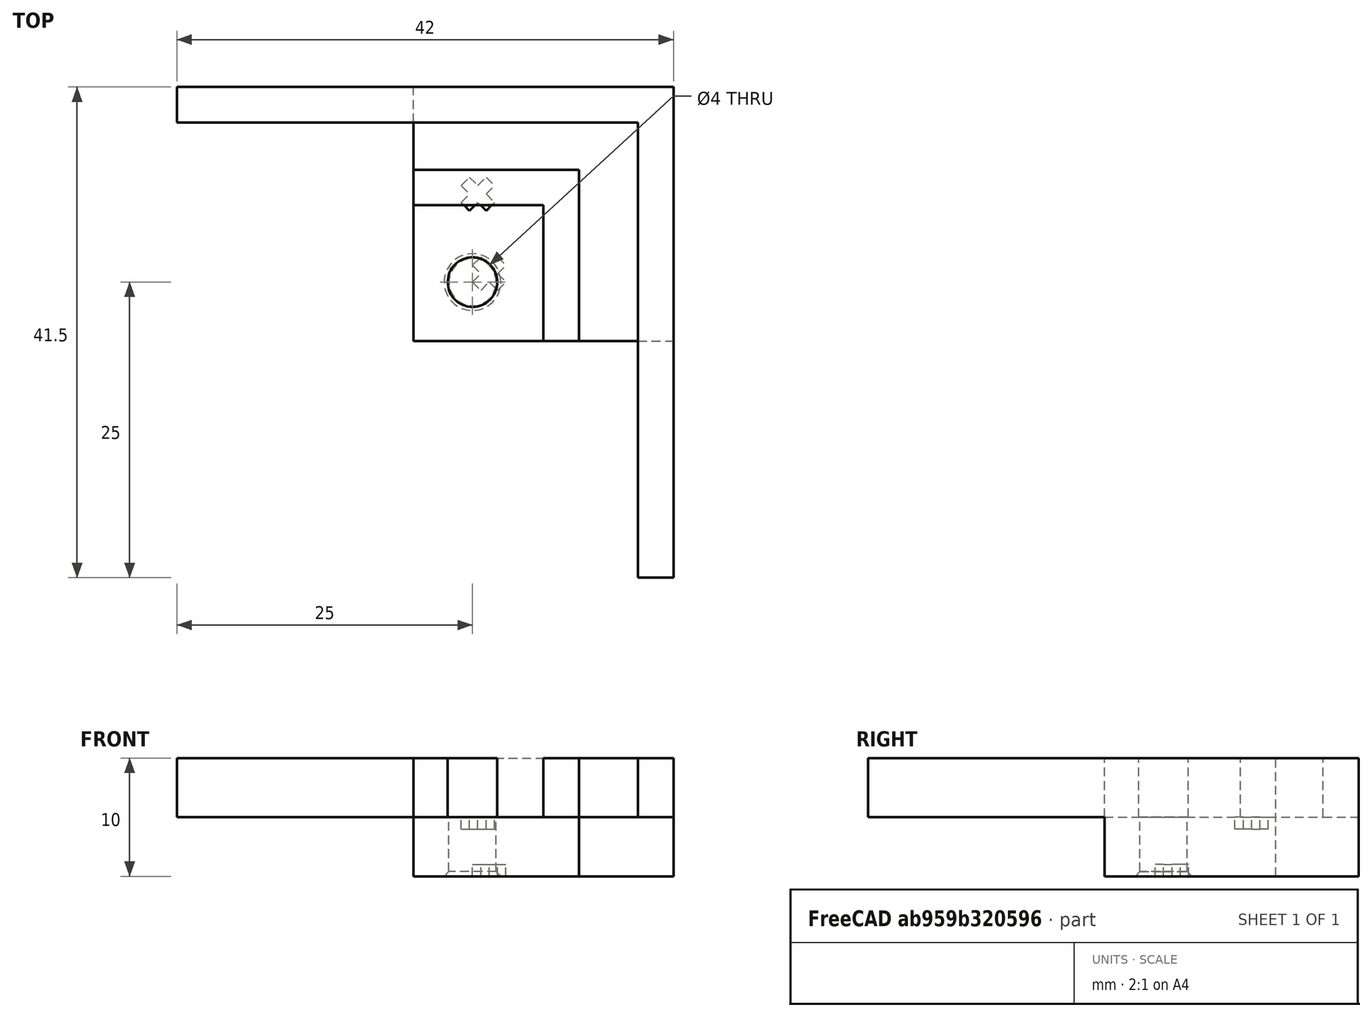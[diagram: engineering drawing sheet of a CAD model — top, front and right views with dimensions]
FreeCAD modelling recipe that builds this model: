
FCSTD DOCUMENT  (FreeCAD 0.18R16146 (Git))
Label: drill-template
License: All rights reserved
LicenseURL: http://en.wikipedia.org/wiki/All_rights_reserved
objects: Part::Box×10, Part::MultiFuse×3, Part::Cylinder×2, Part::Cut×2, Part::Chamfer×1, Part::Feature×1
note: 19 computed .brp shape members not serialized (recipe doc carries the construction recipe); baked Part::Feature solids carry a one-line shape summary decoded from their .brp

FEATURE [Part::Box] Box  label="Cube"
  AttacherType = Attacher::AttachEngine3D
  Height = 5
  Length = 11
  Placement = pos=(-5,-5,0) rot=(0,0,1;0rad)
  Width = 11.5
FEATURE [Part::Cylinder] Cylinder
  Angle = 360
  AttacherType = Attacher::AttachEngine3D
  Height = 10
  Radius = 2.1
FEATURE [Part::Box] Box001  label="Cube001"
  AttacherType = Attacher::AttachEngine3D
  Height = 10
  Length = 11
  Placement = pos=(-5,6.5,0) rot=(0,0,1;0rad)
  Width = 3
FEATURE [Part::Box] Box002  label="Cube002"
  AttacherType = Attacher::AttachEngine3D
  Height = 10
  Length = 3
  Placement = pos=(6,-5,0) rot=(0,0,1;0rad)
  Width = 14.5
FEATURE [Part::MultiFuse] Fusion
  Shapes = -> [Box001,Cylinder,Box002,Box]
FEATURE [Part::Box] Box003  label="Cube003"
  AttacherType = Attacher::AttachEngine3D
  Height = 5
  Length = 19
  Placement = pos=(-5,-5,0) rot=(0,0,1;0rad)
  Width = 18.5
FEATURE [Part::Cylinder] Cylinder001
  Angle = 360
  AttacherType = Attacher::AttachEngine3D
  Height = 10
  Radius = 2
FEATURE [Part::Box] Box004  label="Cube004"
  AttacherType = Attacher::AttachEngine3D
  Height = 10
  Length = 22
  Placement = pos=(-5,13.5,0) rot=(0,0,1;0rad)
  Width = 3
FEATURE [Part::Box] Box005  label="Cube005"
  AttacherType = Attacher::AttachEngine3D
  Height = 10
  Length = 3
  Placement = pos=(14,-5,0) rot=(0,0,1;0rad)
  Width = 21.5
FEATURE [Part::Box] Box006  label="Cube006"
  AttacherType = Attacher::AttachEngine3D
  Height = 5
  Length = 3
  Placement = pos=(14,-25,5) rot=(0,0,1;0rad)
  Width = 20
FEATURE [Part::Box] Box007  label="Cube007"
  AttacherType = Attacher::AttachEngine3D
  Height = 5
  Length = 20
  Placement = pos=(-25,13.5,5) rot=(0,0,1;0rad)
  Width = 3
FEATURE [Part::MultiFuse] Fusion001
  Shapes = -> [Box003,Box004,Box006,Box005,Box007]
FEATURE [Part::Cut] Cut
  Base = -> Fusion001
  Tool = -> Cylinder001
FEATURE [Part::Chamfer] Chamfer  label="355"
  Base = -> Cut
  Edges = 1 edges r=0.4: [Edge16]
FEATURE [Part::Box] Box008  label="Cube008"
  AttacherType = Attacher::AttachEngine3D
  Height = 1
  Length = 3
  Placement = pos=(-1,1,0) rot=(0,0,1;0rad)
  Width = 1
FEATURE [Part::Box] Box009  label="Cube009"
  AttacherType = Attacher::AttachEngine3D
  Height = 1
  Length = 1
  Width = 3
FEATURE [Part::MultiFuse] Fusion002  label="x"
  Placement = pos=(0,0,0) rot=(0,0,1;5.49779rad)
  Shapes = -> [Box009,Box008]
FEATURE [Part::Feature] Fusion002001  label="x001"
  Placement = pos=(-0.965926,6.74118,4) rot=(0,0,1;0.261799rad)
  shape: bbox 2.828 x 2.828 x 1 mm, 14 faces (baked)
FEATURE [Part::Cut] Cut001
  Base = -> Chamfer
  Tool = -> Fusion002001
